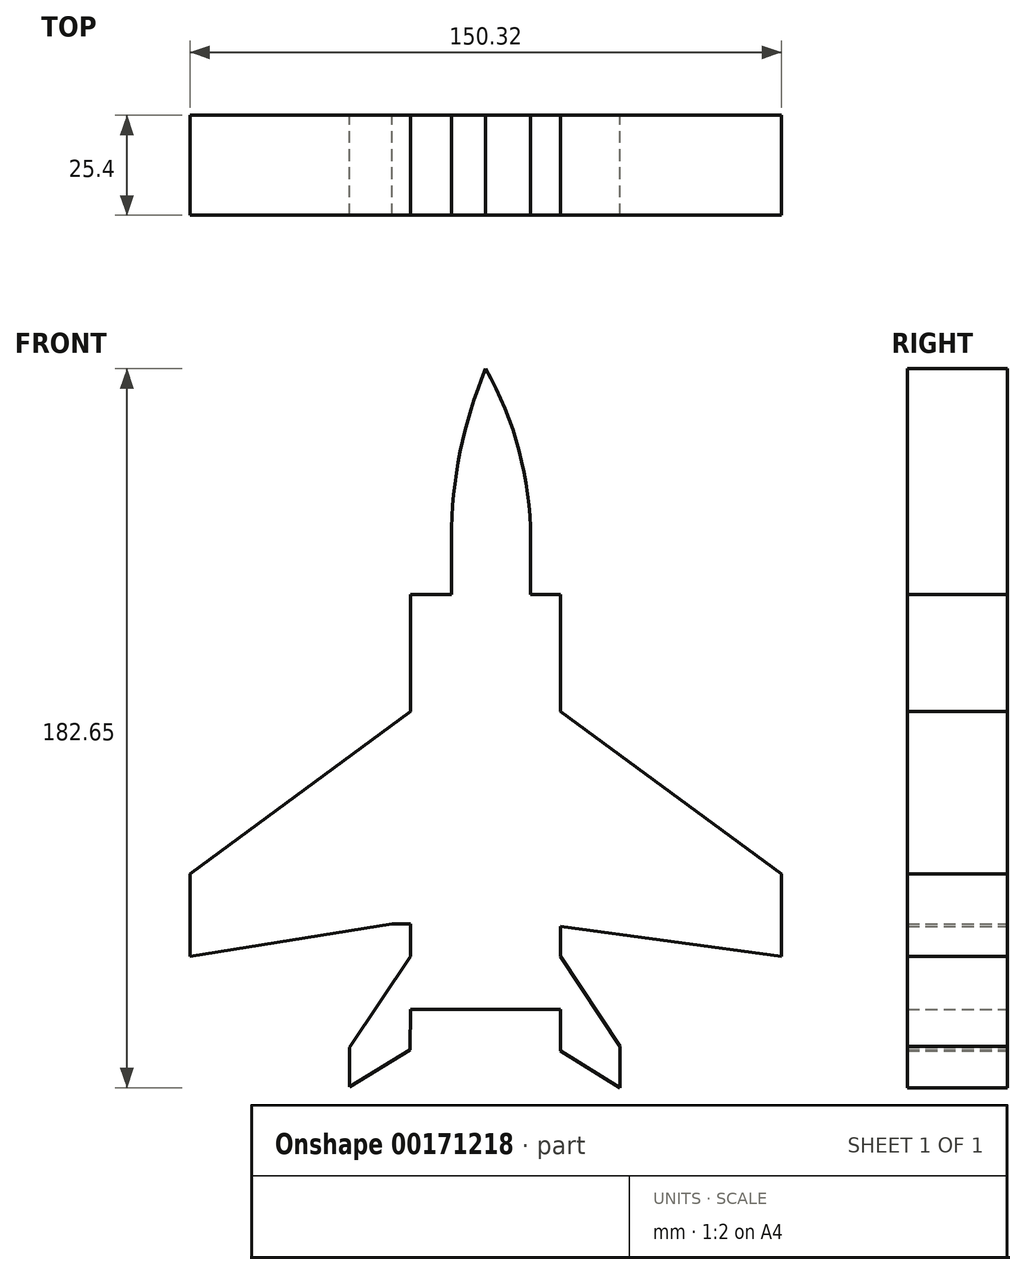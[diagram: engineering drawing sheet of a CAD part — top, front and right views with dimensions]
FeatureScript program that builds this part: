
annotation { "Feature Type Name" : "Feature", "Feature Type Description" : "" }
export const myFeature = defineFeature(function(context is Context, id is Id, definition is map)
    precondition{}
    {
        {
            var Q0;
            Q0=qCreatedBy(makeId("Front.planeOp"),FACE);
            var sketch = newSketch(context, id + "F0", { "sketchPlane" : qUnion([Q0])});
            skLineSegment(sketch, "E0.bottom", {"start": v(19.05, -52.7) * mm, "end": v(-19.05, -52.7) * mm});
            skLineSegment(sketch, "E0.top", {"start": v(19.05, 52.7) * mm, "end": v(11.36, 52.7) * mm});
            skLineSegment(sketch, "E0.left", {"start": v(19.05, -39.2) * mm, "end": v(19.05, -30.98) * mm});
            skLineSegment(sketch, "E0.right", {"start": v(-19.05, -39.2) * mm, "end": v(-19.05, -30.98) * mm});
            skPoint(sketch, "E0.middle", {"position": v(0, 0) * mm});
            skLineSegment(sketch, "E1", {"start": v(19.05, -52.7) * mm, "end": v(19.05, -63.28) * mm});
            skLineSegment(sketch, "E2", {"start": v(-19.05, -52.7) * mm, "end": v(-19.18, -63.05) * mm});
            skLineSegment(sketch, "E3", {"start": v(-19.18, -63.05) * mm, "end": v(-34.61, -72.38) * mm});
            skLineSegment(sketch, "E4", {"start": v(19.05, -63.28) * mm, "end": v(34.08, -72.6) * mm});
            skLineSegment(sketch, "E5", {"start": v(-34.61, -72.38) * mm, "end": v(-34.61, -62.4) * mm});
            skLineSegment(sketch, "E6", {"start": v(34.08, -72.6) * mm, "end": v(34.08, -62.17) * mm});
            skLineSegment(sketch, "E7", {"start": v(-34.61, -62.4) * mm, "end": v(-19.05, -39.2) * mm});
            skLineSegment(sketch, "E8", {"start": v(34.08, -62.17) * mm, "end": v(19.05, -39.2) * mm});
            skPoint(sketch, "E9.orphan", {"position": v(-34.61, -39.2) * mm});
            skLineSegment(sketch, "E10", {"start": v(-23.77, -30.98) * mm, "end": v(-19.05, -30.98) * mm});
            skLineSegment(sketch, "E11", {"start": v(-23.77, -30.98) * mm, "end": v(-75.16, -39.2) * mm});
            skLineSegment(sketch, "E12", {"start": v(14.1, -30.98) * mm, "end": v(75.16, -39.2) * mm});
            skLineSegment(sketch, "E13", {"start": v(75.16, -18.33) * mm, "end": v(75.16, -39.2) * mm});
            skLineSegment(sketch, "E14", {"start": v(-75.16, -18.33) * mm, "end": v(-19.05, 23.03) * mm});
            skLineSegment(sketch, "E15", {"start": v(75.16, -18.33) * mm, "end": v(19.05, 23.03) * mm});
            skLineSegment(sketch, "E16.trimOffspring", {"start": v(14.1, -30.98) * mm, "end": v(19.05, -30.98) * mm});
            skPoint(sketch, "E17.orphan", {"position": v(75.16, 23.03) * mm});
            skPoint(sketch, "E18.orphan", {"position": v(-75.16, 23.03) * mm});
            skLineSegment(sketch, "E19", {"start": v(-8.7, 52.7) * mm, "end": v(-8.7, 67) * mm});
            skLineSegment(sketch, "E20", {"start": v(11.36, 67) * mm, "end": v(11.36, 52.7) * mm});
            skPoint(sketch, "E21", {"position": v(0, 110.05) * mm});
            skArc(sketch, "E22", {"start": v(0, 110.05) * mm, "mid": v(-6.5, 88.96) * mm, "end": v(-8.7, 67) * mm});
            skArc(sketch, "E23", {"start": v(11.36, 67) * mm, "mid": v(8.48, 89.26) * mm, "end": v(0, 110.05) * mm});
            skLineSegment(sketch, "E24.trimOffspring", {"start": v(-8.7, 52.7) * mm, "end": v(-19.05, 52.7) * mm});
            skLineSegment(sketch, "E25", {"start": v(-75.16, -39.2) * mm, "end": v(-75.16, -18.33) * mm});
            skLineSegment(sketch, "E26.trimOffspring", {"start": v(19.05, 23.03) * mm, "end": v(19.05, 52.7) * mm});
            skLineSegment(sketch, "E27.trimOffspring", {"start": v(-19.05, 23.03) * mm, "end": v(-19.05, 52.7) * mm});
            skSolve(sketch);
        }
        {
            var Q0;
            Q0=makeQuery(id+"F0.imprint","IMPRINT",FACE,{"disambiguationData":[TD([[makeQuery(id+"F0.imprint","IMPRINT",EDGE,{"derivedFrom":sQuery(id+"F0.wireOp",EDGE,"E0.bottom")}),-1.0]])]});
            var Q1;
            {var subQ0=sQuery(id+"F0.wireOp",EDGE,"E16.trimOffspring");Q1=makeQuery(id+"F0.imprint","IMPRINT",FACE,{"disambiguationData":[TD([[makeQuery(id+"F0.imprint","IMPRINT",EDGE,{"derivedFrom":subQ0}),-1.0]])]});}
            extrude(context, id + "F1", {"entities" : qUnion([Q0, Q1]), "endBound" : BoundingType.SYMMETRIC, "depth" : 25.4 * mm});
        }
    });
